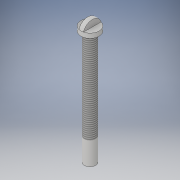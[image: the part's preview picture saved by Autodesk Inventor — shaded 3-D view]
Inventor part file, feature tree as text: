
AUTODESK INVENTOR PART (.ipt)
format: ipt  version: 2019 (Build 230136000, 136)  size: 135,168 bytes
history: native  units: in
note: dims shown in document units (in); Inventor stores cm internally (conversion verified against a paired STEP export)
features: sketch x4, extrude x3, revolve x1, thread x1
ambient origin geometry x8: Origin, YZ Plane, XZ Plane, XY Plane, X Axis, Y Axis, Z Axis, Center Point
bodies: Solid1 (feature_tree)
feature tree (9):
  extrude  "Extrusion1"  Depth=1.9685in TaperAngle=0.0deg
  extrude  "Extrusion2"  Depth=0.3779in
  extrude  "Extrusion3"  Depth=0.0787in TaperAngle=0.0deg
  revolve  "Revolution5"  [1 undecoded]
  thread  "Thread4"  [1 undecoded]
  sketch  "Sketch1"  dims[d0=0.1969in d1=1.9685in d2=0.0in]
  sketch  "Sketch9"  dims[d23=0.3779in d44=0.3779in]
  sketch  "Sketch10"  dims[d56=0.315in d57=0.0787in d58=0.0in]
  sketch  "Sketch11"  dims[d59=0.315in d60=0.1181in d61=0.0787in d62=0.0in d65=0.1969in d67=90.0deg d68=0.0787in d69=1.5748in d70=0.0in]
note: 2 required parameter values undecoded (feature->parameter linkage not recoverable at this tier; creation-order binding heuristic only, values carry confidence <= 0.55)